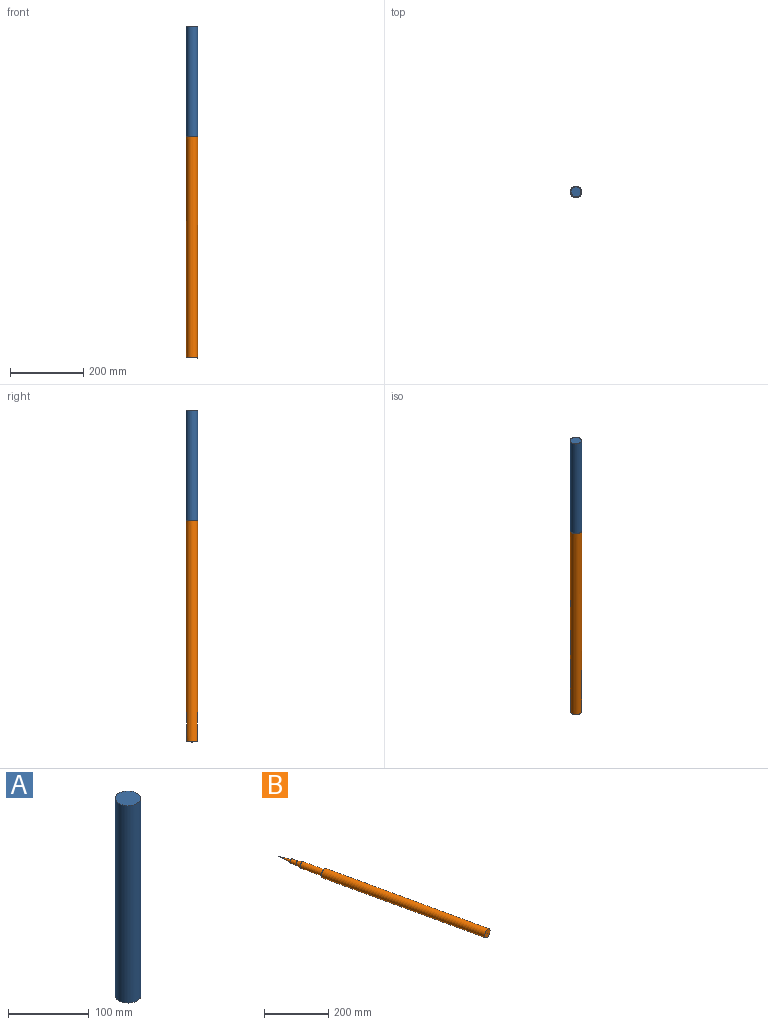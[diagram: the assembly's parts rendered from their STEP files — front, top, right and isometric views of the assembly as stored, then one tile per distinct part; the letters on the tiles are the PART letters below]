
ASSEMBLY  parts=2 mates=1
PART A: 5 faces, bbox 31.4x31.4x300 mm
  f0: cylinder r=15.7mm len=300mm, axis (0,0,-1), area 29593.8mm2, adj f1,f2
  f1: plane 31.4x31.4mm, normal (0,0,1), area 774.4mm2, adj f0
  f2: plane 31.4x31.4mm, normal (0,0,-1), area 184.7mm2, adj f0,f3
  f3: cylinder r=13.7mm len=298mm, axis (0,0,-1), area 25651.7mm2, adj f2,f4
  f4: plane 27.4x27.4mm, normal (0,0,-1), area 589.6mm2, adj f3
PART B: 8 faces, bbox 181.4x759.9x31.4 mm
  f0: cone r=0mm half-angle=89.9deg, axis (0.22,-0.98,0), area 706.9mm2, adj f7
  f1: cone r=4.13mm half-angle=4.9deg, axis (0.22,-0.98,0), area 631.5mm2, adj f2
  f2: cone r=6.91mm half-angle=89.9deg, axis (0.22,-0.98,0), area 96.4mm2, adj f1,f3
  f3: cone r=7.05mm half-angle=0.3deg, axis (0.22,-0.98,0), area 999.9mm2, adj f2,f4
  f4: cone r=11.02mm half-angle=12.4deg, axis (0.22,-0.98,0), area 1047.1mm2, adj f3,f5
  f5: cone r=10.92mm half-angle=0.1deg, axis (-0.22,0.98,0), area 5581.3mm2, adj f4,f6
  f6: cone r=15.71mm half-angle=89.9deg, axis (0.22,-0.98,0), area 400.6mm2, adj f5,f7
  f7: cone r=15mm half-angle=0.1deg, axis (-0.22,0.98,0), area 58326.3mm2, adj f0,f6
PLACE A t=(-71.15,153.5,-18.96)mm
PLACE B rot(axis=(0.99,0.11,-0.11),90.7deg) t=(-71.86,153.5,-22.27)mm
MATE cylindrical B.f1 <-> A.f0  axis (0,0,1) through (-71.15,153.5,-18.96)mm
